annotation { "Feature Type Name" : "Feature", "Feature Type Description" : "" }
export const myFeature = defineFeature(function(context is Context, id is Id, definition is map)
    precondition{}
    {
        {
            var Q0;
            Q0=qCreatedBy(makeId("Top.planeOp"),FACE);
            var sketch = newSketch(context, id + "F0", { "sketchPlane" : qUnion([Q0])});
            skLineSegment(sketch, "E0.bottom", {"start": v(-15, 14) * mm, "end": v(15, 14) * mm});
            skLineSegment(sketch, "E0.top", {"start": v(-15, -14) * mm, "end": v(15, -14) * mm});
            skLineSegment(sketch, "E0.left", {"start": v(-25, 4) * mm, "end": v(-25, -4) * mm});
            skLineSegment(sketch, "E0.right", {"start": v(25, 4) * mm, "end": v(25, -4) * mm});
            skPoint(sketch, "E1.visualSharp", {"position": v(-25, 14) * mm});
            skArc(sketch, "E1.filletArc", {"start": v(-15, 14) * mm, "mid": v(-22.07, 11.07) * mm, "end": v(-25, 4) * mm});
            skPoint(sketch, "E2.visualSharp", {"position": v(-25, -14) * mm});
            skArc(sketch, "E2.filletArc", {"start": v(-25, -4) * mm, "mid": v(-22.07, -11.07) * mm, "end": v(-15, -14) * mm});
            skPoint(sketch, "E3.visualSharp", {"position": v(25, -14) * mm});
            skArc(sketch, "E3.filletArc", {"start": v(15, -14) * mm, "mid": v(22.07, -11.07) * mm, "end": v(25, -4) * mm});
            skPoint(sketch, "E4.visualSharp", {"position": v(25, 14) * mm});
            skArc(sketch, "E4.filletArc", {"start": v(25, 4) * mm, "mid": v(22.07, 11.07) * mm, "end": v(15, 14) * mm});
            skCircle(sketch, "E5", {"center": v(-20, 0) * mm, "radius": 3 * mm});
            skSolve(sketch);
        }
        {
            var Q0;
            Q0=makeQuery(id+"F0.imprint","IMPRINT",FACE,{"disambiguationData":[TD([[makeQuery(id+"F0.imprint","IMPRINT",EDGE,{"derivedFrom":sQuery(id+"F0.wireOp",EDGE,"E0.bottom")}),-1.0]])]});
            extrude(context, id + "F1", {"entities" : qUnion([Q0]), "depth" : 3 * mm, "offsetDistance" : 25 * mm});
        }
        {
            var Q0;
            Q0=makeQuery(id+"F1.opExtrude","CAP_FACE",FACE,{"disambiguationData":[OSD([sQuery(id+"F0.wireOp",EDGE,"E0.bottom"),sQuery(id+"F0.wireOp",EDGE,"E0.top"),sQuery(id+"F0.wireOp",EDGE,"E0.left"),sQuery(id+"F0.wireOp",EDGE,"E0.right"),sQuery(id+"F0.wireOp",EDGE,"E1.filletArc"),sQuery(id+"F0.wireOp",EDGE,"E2.filletArc"),sQuery(id+"F0.wireOp",EDGE,"E3.filletArc"),sQuery(id+"F0.wireOp",EDGE,"E4.filletArc"),sQuery(id+"F0.wireOp",EDGE,"E5")])],"isStart":true});
            var sketch = newSketch(context, id + "F2", { "sketchPlane" : qUnion([Q0])});
            skText(sketch, "E6", { "text": "PLAYA", "fontName": "OpenSans-Bold.ttf"});
            skText(sketch, "E7", { "text": "DEL CARMEN", "fontName": "OpenSans-Bold.ttf"});
            skText(sketch, "E8", { "text": "2017", "fontName": "OpenSans-Bold.ttf"});
            const initialGuessF2  = {"E6": [-0.01157, 0.00635, 1, 0, 0.006], "E7": [-0.01665, 0.0004, 1, 0, 0.0045], "E8": [-0.0117, -0.01103, 1, 0, 0.0092]};
            skSetInitialGuess(sketch, initialGuessF2);
            skSolve(sketch);
        }
        {
            var Q0;
            Q0 = qSketchRegion(id + "F2", true);
            extrude(context, id + "F3", {"entities" : qUnion([Q0]), "operationType" : NewBodyOperationType.REMOVE, "oppositeDirection" : true, "depth" : 1 * mm, "offsetDistance" : 25 * mm});
        }
        {
            var Q0;
            Q0=makeQuery(id+"F1.opExtrude","CAP_FACE",FACE,{"disambiguationData":[OSD([sQuery(id+"F0.wireOp",EDGE,"E0.bottom"),sQuery(id+"F0.wireOp",EDGE,"E0.top"),sQuery(id+"F0.wireOp",EDGE,"E0.left"),sQuery(id+"F0.wireOp",EDGE,"E0.right"),sQuery(id+"F0.wireOp",EDGE,"E1.filletArc"),sQuery(id+"F0.wireOp",EDGE,"E2.filletArc"),sQuery(id+"F0.wireOp",EDGE,"E3.filletArc"),sQuery(id+"F0.wireOp",EDGE,"E4.filletArc"),sQuery(id+"F0.wireOp",EDGE,"E5")])],"isStart":false});
            var sketch = newSketch(context, id + "F4", { "sketchPlane" : qUnion([Q0])});
            skText(sketch, "E9", { "text": "Cerrado Pino 7\n", "fontName": "OpenSans-Bold.ttf"});
            skText(sketch, "E10", { "text": "12 Col. Bosque\n", "fontName": "OpenSans-Bold.ttf"});
            skText(sketch, "E11", { "text": "Real", "fontName": "OpenSans-Bold.ttf"});
            skText(sketch, "E12", { "text": "19-8407-8767", "fontName": "OpenSans-Bold.ttf"});
            const initialGuessF4  = {"E9": [-0.02022, 0.00696, 1, 0, 0.004], "E10": [-0.01736, 0.00183, 1, 0, 0.004], "E11": [0.0081, -0.00353, 1, 0, 0.004], "E12": [-0.02128, -0.00983, 1, 0, 0.00485]};
            skSetInitialGuess(sketch, initialGuessF4);
            skSolve(sketch);
        }
        {
            var Q0;
            Q0 = qSketchRegion(id + "F4", true);
            extrude(context, id + "F5", {"entities" : qUnion([Q0]), "operationType" : NewBodyOperationType.REMOVE, "oppositeDirection" : true, "depth" : 1 * mm, "offsetDistance" : 25 * mm});
        }
    });